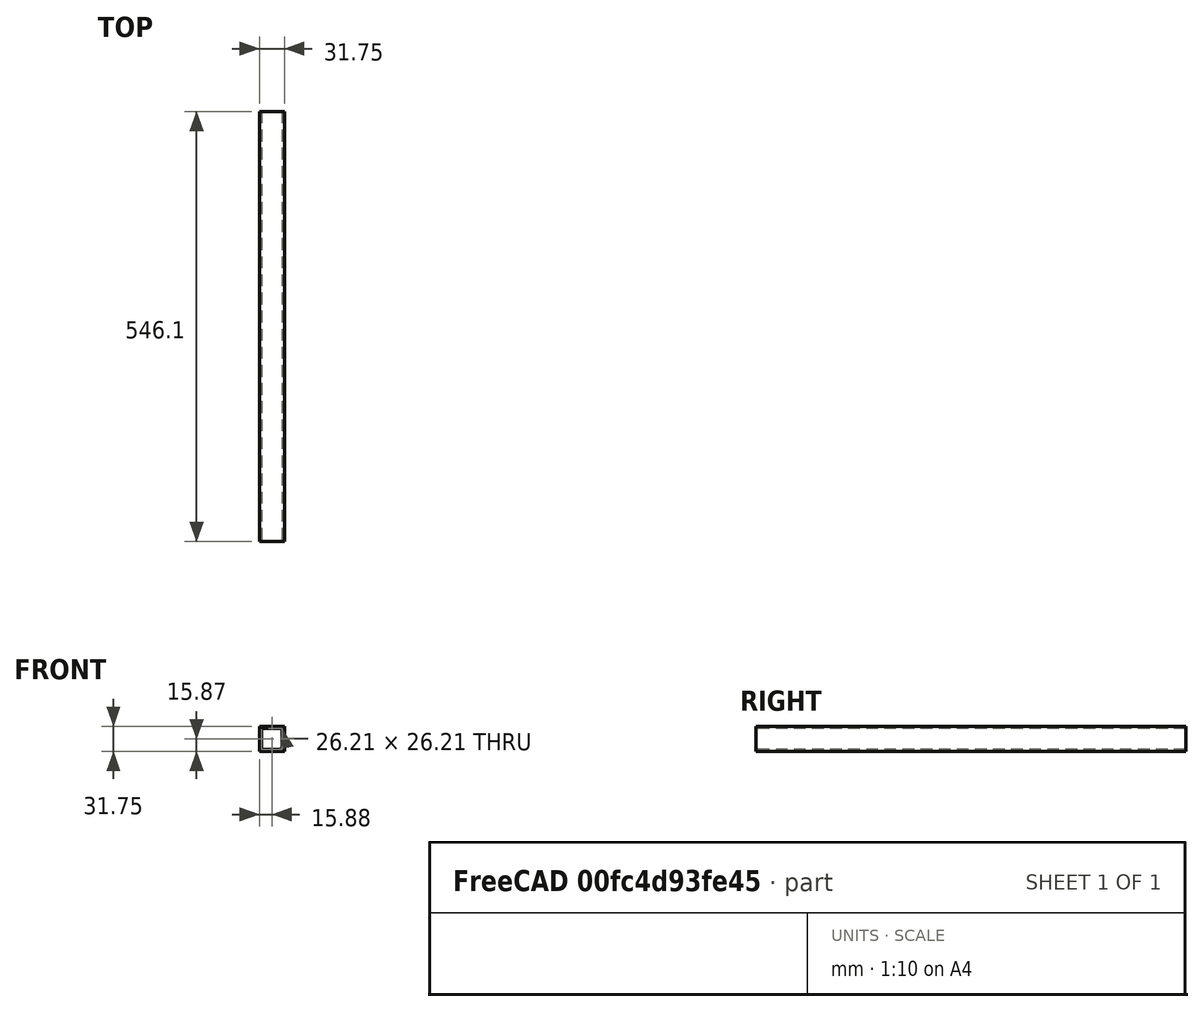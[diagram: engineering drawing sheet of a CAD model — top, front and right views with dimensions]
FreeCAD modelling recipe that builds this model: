
FCSTD DOCUMENT  (FreeCAD 0.16R6062 (Git))
Label: Chassis-Bottom-Part-5
License: All rights reserved
LicenseURL: http://en.wikipedia.org/wiki/All_rights_reserved
objects: Sketcher::SketchObject×1, PartDesign::Pad×1
note: 3 computed .brp shape members not serialized (recipe doc carries the construction recipe); baked Part::Feature solids carry a one-line shape summary decoded from their .brp

FEATURE [Sketcher::SketchObject] Sketch
  Placement = pos=(0,0,0) rot=(-1,0,0;4.71239rad)
  sketch-geometry (8):
    g0: LineSegment StartX=-15.875 StartY=15.875 StartZ=0 EndX=15.875 EndY=15.875 EndZ=0
    g1: LineSegment StartX=15.875 StartY=15.875 StartZ=0 EndX=15.875 EndY=-15.875 EndZ=0
    g2: LineSegment StartX=15.875 StartY=-15.875 StartZ=0 EndX=-15.875 EndY=-15.875 EndZ=0
    g3: LineSegment StartX=-15.875 StartY=-15.875 StartZ=0 EndX=-15.875 EndY=15.875 EndZ=0
    g4: LineSegment StartX=-13.1064 StartY=13.1064 StartZ=0 EndX=13.1064 EndY=13.1064 EndZ=0
    g5: LineSegment StartX=13.1064 StartY=13.1064 StartZ=0 EndX=13.1064 EndY=-13.1064 EndZ=0
    g6: LineSegment StartX=13.1064 StartY=-13.1064 StartZ=0 EndX=-13.1064 EndY=-13.1064 EndZ=0
    g7: LineSegment StartX=-13.1064 StartY=-13.1064 StartZ=0 EndX=-13.1064 EndY=13.1064 EndZ=0
  constraints (22):
    c: Coincident(g0,g1)
    c: Coincident(g1,g2)
    c: Coincident(g2,g3)
    c: Coincident(g3,g0)
    c: Horizontal(g0)
    c: Horizontal(g2)
    c: Vertical(g1)
    c: Vertical(g3)
    c: Equal(g1,g2)
    c: DistanceX(g0) = 31.75
    c: Symmetric(g0,g1,g-1)
    c: Coincident(g4,g5)
    c: Coincident(g5,g6)
    c: Coincident(g6,g7)
    c: Coincident(g7,g4)
    c: Horizontal(g4)
    c: Horizontal(g6)
    c: Vertical(g5)
    c: Vertical(g7)
    c: Equal(g6,g5)
    c: DistanceX(g4) = 26.2128
    c: Symmetric(g4,g5,g-1)
FEATURE [PartDesign::Pad] Pad
  Length = 546.1
  Length2 = 100
  Placement = pos=(0,0,0) rot=(-1,0,0;4.71239rad)
  Sketch = -> Sketch
  Type = 0
